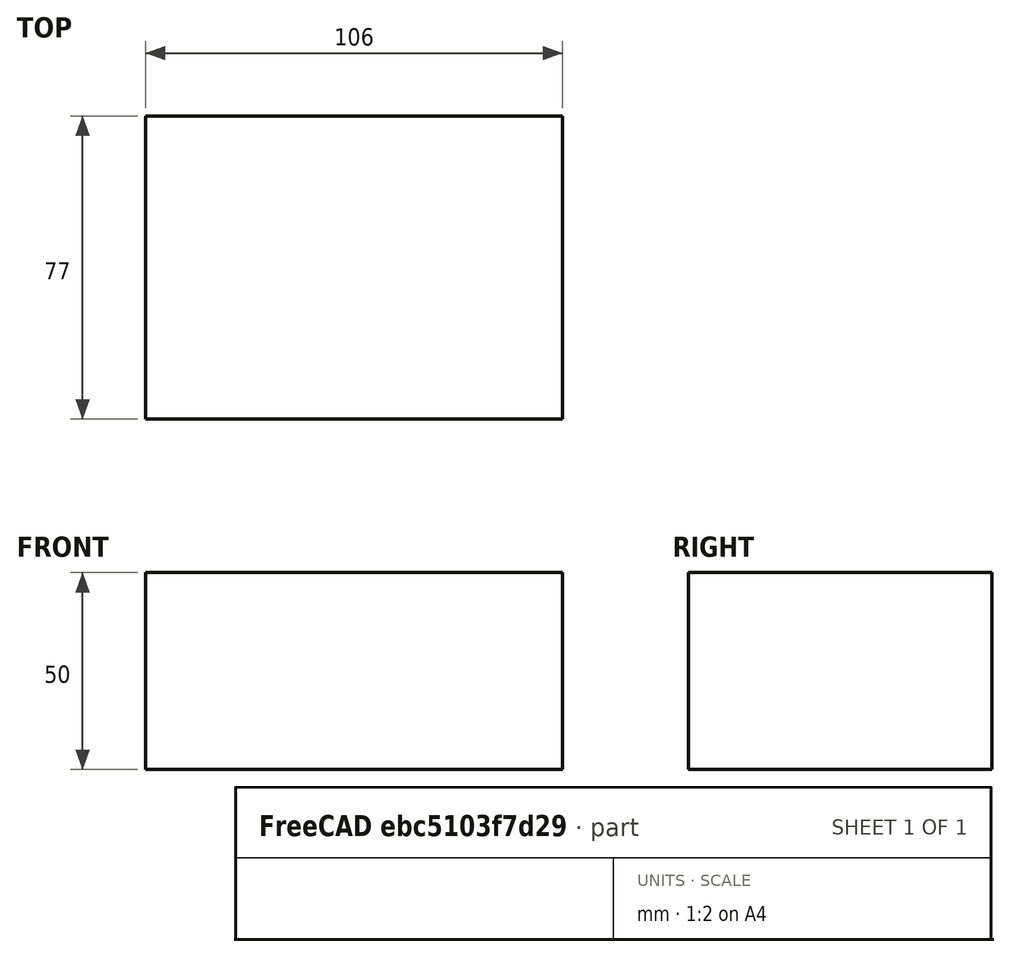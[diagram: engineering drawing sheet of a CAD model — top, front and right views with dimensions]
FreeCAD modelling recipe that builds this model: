
FCSTD DOCUMENT  (FreeCAD 1.0R39109 (Git))
Label: digitanimal_ref
License: All rights reserved
LicenseURL: http://en.wikipedia.org/wiki/All_rights_reserved
objects: Sketcher::SketchObject×1, PartDesign::Pad×1, PartDesign::Body×1
note: 6 computed .brp shape members not serialized (recipe doc carries the construction recipe); baked Part::Feature solids carry a one-line shape summary decoded from their .brp

FEATURE [Sketcher::SketchObject] Sketch
  ArcFitTolerance = 1e-06
  AttachmentSupport = -> [XY_Plane]
  FullyConstrained = true
  MakeInternals = false
  MapMode = 5
  sketch-geometry (4):
    g0: LineSegment StartX=-53 StartY=38.5 StartZ=0 EndX=-53 EndY=-38.5 EndZ=0
    g1: LineSegment StartX=-53 StartY=-38.5 StartZ=0 EndX=53 EndY=-38.5 EndZ=0
    g2: LineSegment StartX=53 StartY=-38.5 StartZ=0 EndX=53 EndY=38.5 EndZ=0
    g3: LineSegment StartX=53 StartY=38.5 StartZ=0 EndX=-53 EndY=38.5 EndZ=0
  constraints (11):
    c: Coincident(g0,g1)
    c: Coincident(g1,g2)
    c: Coincident(g2,g3)
    c: Coincident(g3,g0)
    c: Vertical(g0)
    c: Vertical(g2)
    c: Horizontal(g1)
    c: Horizontal(g3)
    c: Symmetric(g0,g1,g-1)
    c: DistanceX(g3,g3) = 106
    c: DistanceY(g0,g0) = 77
FEATURE [PartDesign::Pad] Pad
  Direction = (0,0,1)
  Length = 50
  Length2 = 10
  Profile = -> Sketch
  ReferenceAxis = -> Sketch [N_Axis]
  Suppressed = false
  Type = 0
FEATURE [PartDesign::Body] Body
  AllowCompound = false
  Group = -> [Sketch,Pad]
  Origin = -> Origin
  Tip = -> Pad
